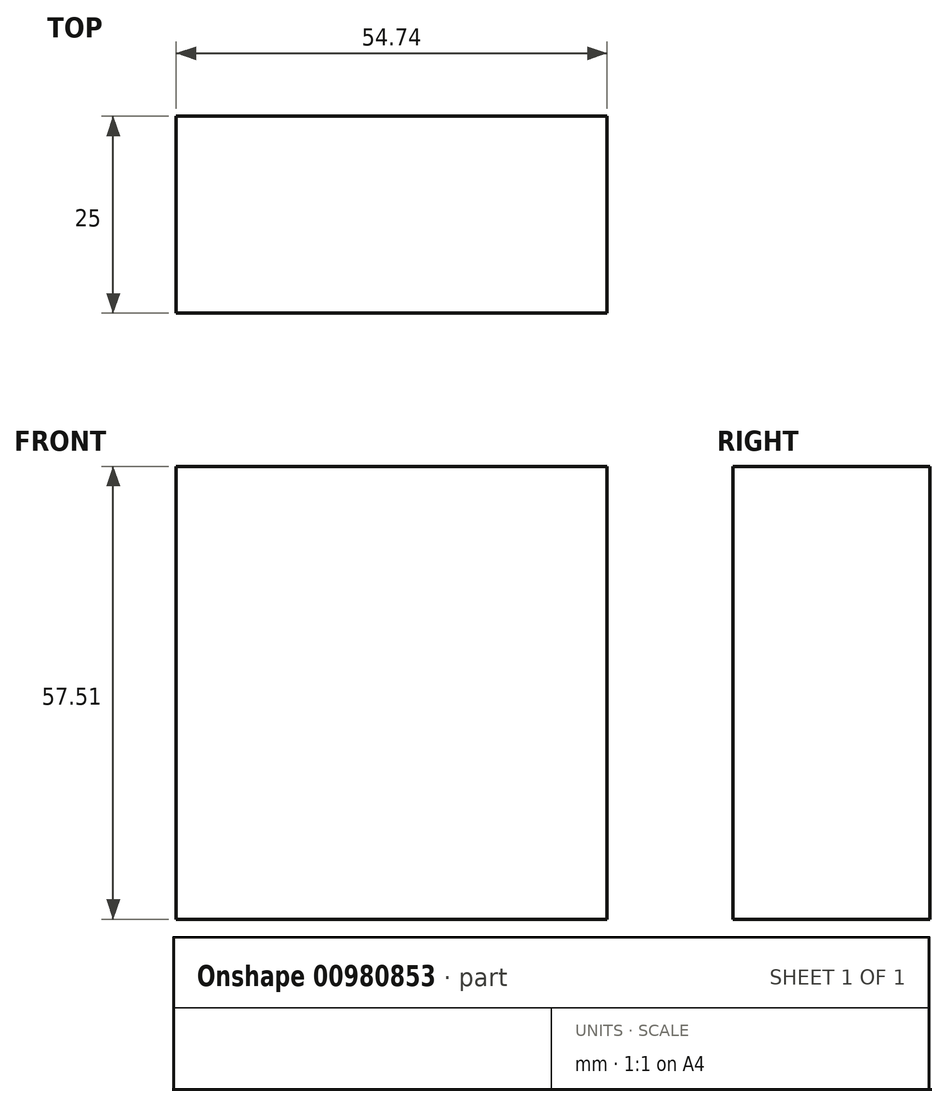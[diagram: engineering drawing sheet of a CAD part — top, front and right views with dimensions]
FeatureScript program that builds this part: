
annotation { "Feature Type Name" : "Feature", "Feature Type Description" : "" }
export const myFeature = defineFeature(function(context is Context, id is Id, definition is map)
    precondition{}
    {
        {
            var Q0;
            Q0=qCreatedBy(makeId("Front.planeOp"),FACE);
            var sketch = newSketch(context, id + "F0", { "sketchPlane" : qUnion([Q0])});
            skLineSegment(sketch, "E0.bottom", {"start": v(-130.68, 0) * mm, "end": v(-75.94, 0) * mm});
            skLineSegment(sketch, "E0.top", {"start": v(-130.68, 57.51) * mm, "end": v(-75.94, 57.51) * mm});
            skLineSegment(sketch, "E0.left", {"start": v(-130.68, 0) * mm, "end": v(-130.68, 57.51) * mm});
            skLineSegment(sketch, "E0.right", {"start": v(-75.94, 0) * mm, "end": v(-75.94, 57.51) * mm});
            skPoint(sketch, "E0.middle", {"position": v(-103.3, 28.76) * mm});
            skSolve(sketch);
        }
        {
            var Q0;
            Q0=makeQuery(id+"F0.imprint","IMPRINT",FACE,{"disambiguationData":[TD([[makeQuery(id+"F0.imprint","IMPRINT",EDGE,{"derivedFrom":sQuery(id+"F0.wireOp",EDGE,"E0.bottom")}),1.0]])]});
            extrude(context, id + "F1", {"entities" : qUnion([Q0]), "depth" : 25 * mm, "offsetDistance" : 25 * mm});
        }
        {
            var Q0;
            Q0=sQuery(id+"F0.wireOp",EDGE,"E0.left");
            extrude(context, id + "F2", {"bodyType" : ToolBodyType.SURFACE, "surfaceEntities" : qUnion([Q0]), "depth" : 52.9 * mm, "offsetDistance" : 25 * mm});
        }
    });
